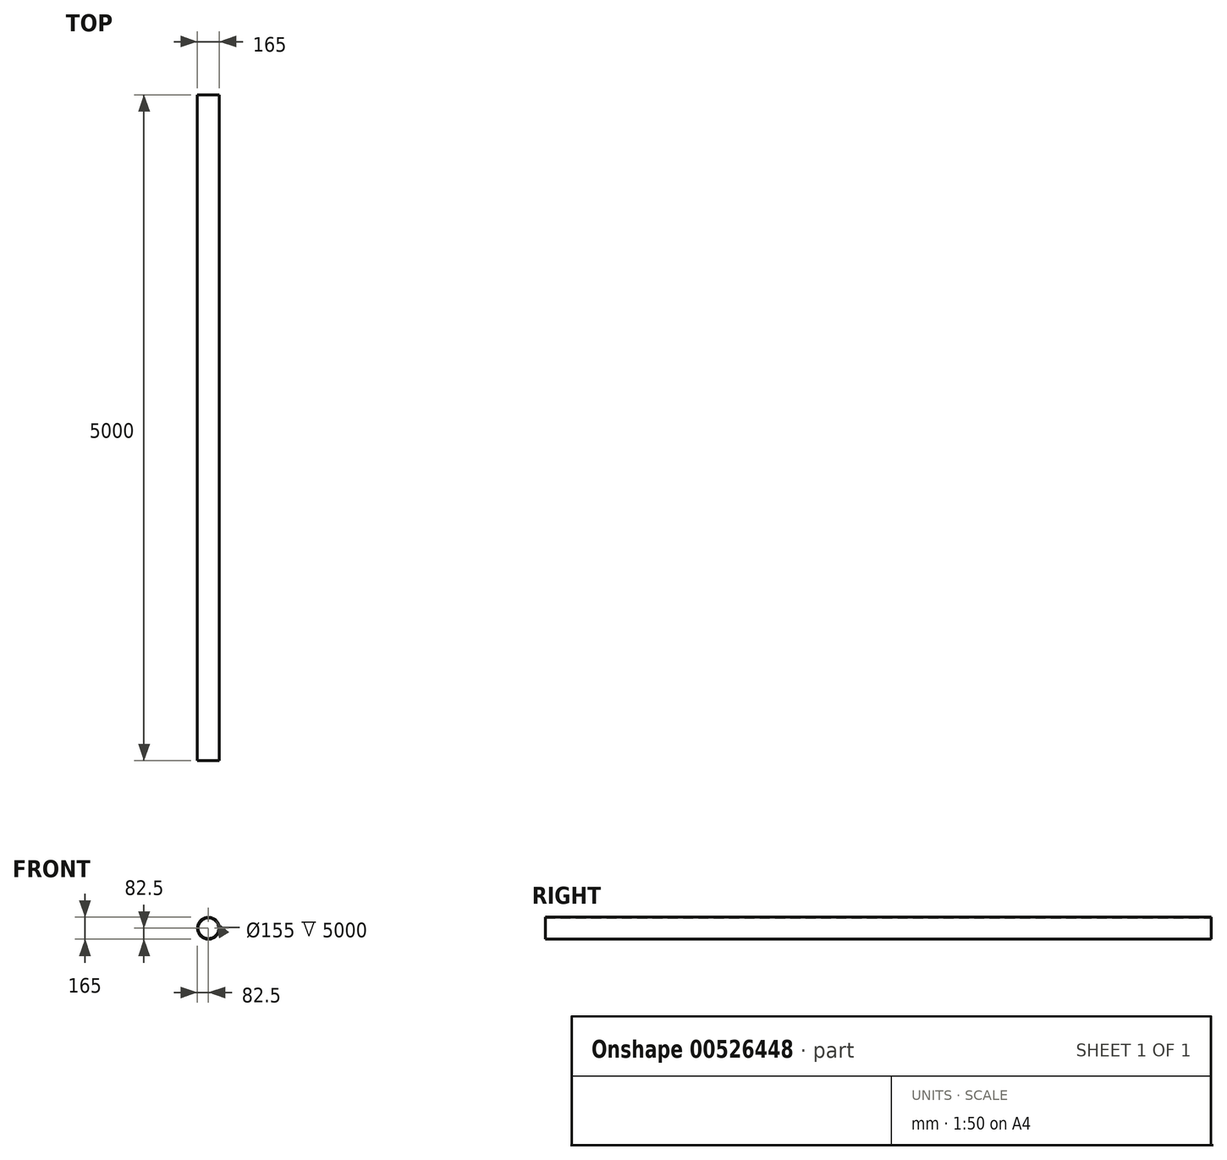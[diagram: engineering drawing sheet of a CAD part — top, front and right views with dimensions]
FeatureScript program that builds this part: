
annotation { "Feature Type Name" : "Feature", "Feature Type Description" : "" }
export const myFeature = defineFeature(function(context is Context, id is Id, definition is map)
    precondition{}
    {
        {
            var Q0;
            Q0=qCreatedBy(makeId("Front.planeOp"),FACE);
            var sketch = newSketch(context, id + "F0", { "sketchPlane" : qUnion([Q0])});
            skCircle(sketch, "E0", {"center": v(0, 0) * mm, "radius": 82.5 * mm});
            skCircle(sketch, "E1", {"center": v(0, 0) * mm, "radius": 77.5 * mm});
            skSolve(sketch);
        }
        {
            var Q0;
            Q0=makeQuery(id+"F0.imprint","IMPRINT",FACE,{"disambiguationData":[TD([[makeQuery(id+"F0.imprint","IMPRINT",EDGE,{"derivedFrom":sQuery(id+"F0.wireOp",EDGE,"E0")}),1.0]])]});
            extrude(context, id + "F1", {"entities" : qUnion([Q0]), "endBound" : BoundingType.SYMMETRIC, "depth" : 5000 * mm, "offsetDistance" : 25 * mm});
        }
    });
